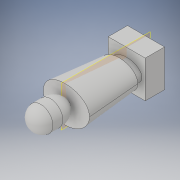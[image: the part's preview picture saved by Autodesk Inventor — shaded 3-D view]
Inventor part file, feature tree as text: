
AUTODESK INVENTOR PART (.ipt)
format: ipt  version: 2017 (Build 210142000, 142)  size: 244,736 bytes
history: native  units: in
note: dims shown in document units (in); Inventor stores cm internally (conversion verified against a paired STEP export)
features: sketch x5, extrude x4, projected_geometry x3, plane x1, revolve x1
ambient origin geometry x8: Origin, YZ Plane, XZ Plane, XY Plane, X Axis, Y Axis, Z Axis, Center Point
bodies: Solid1 (feature_tree)
feature tree (14):
  extrude  "Extrusion1"  Depth=0.575in
  extrude  "Extrusion2"  Depth=0.236in
  extrude  "Extrusion3"  Depth=0.115in TaperAngle=0.0deg
  plane  "Work Plane1"
  extrude  "Extrusion4"  Depth=0.84in
  revolve  "Revolution1"  Angle=90.0deg
  sketch  "Sketch1"  dims[d0=0.575in d1=0.575in]
  sketch  "Sketch2"  dims[d2=0.3in d3=0.0in d4=0.236in]
  sketch  "Sketch3"  dims[d5=0.155in d6=0.115in d7=0.0in]
  sketch  "Sketch4"  dims[d8=0.05in d9=0.84in d10=0.0344in]
  projected_geometry  "Projected Loop1"
  projected_geometry  "Projected Loop2"
  sketch  "Sketch5"  dims[d12=0.84in d13=0.0in d17=90.0deg]
  projected_geometry  "Projected Loop3"
